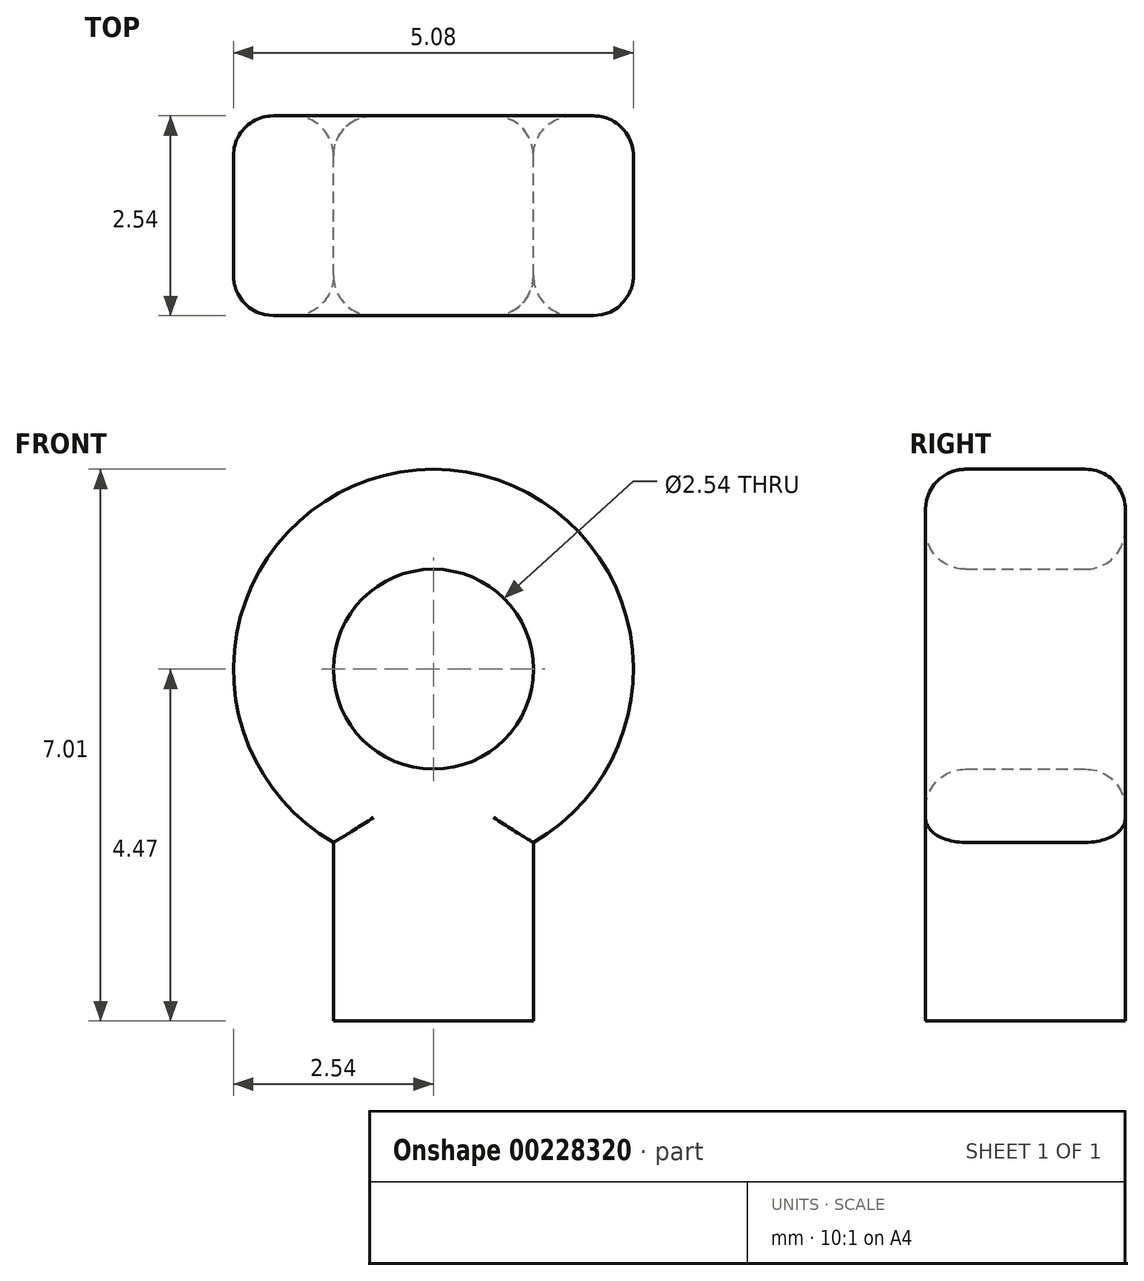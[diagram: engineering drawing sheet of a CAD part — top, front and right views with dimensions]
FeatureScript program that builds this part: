
annotation { "Feature Type Name" : "Feature", "Feature Type Description" : "" }
export const myFeature = defineFeature(function(context is Context, id is Id, definition is map)
    precondition{}
    {
        {
            var Q0;
            Q0=qCreatedBy(makeId("Front.planeOp"),FACE);
            var sketch = newSketch(context, id + "F0", { "sketchPlane" : qUnion([Q0])});
            skArc(sketch, "E0", {"start": v(1.27, -2.2) * mm, "mid": v(0, 2.54) * mm, "end": v(-1.27, -2.2) * mm});
            skCircle(sketch, "E1", {"center": v(0, 0) * mm, "radius": 1.27 * mm});
            skLineSegment(sketch, "E2.0", {"start": v(-1.27, -2.2) * mm, "end": v(-1.27, -4.47) * mm});
            skLineSegment(sketch, "E3.0", {"start": v(1.27, -2.2) * mm, "end": v(1.27, -4.47) * mm});
            skLineSegment(sketch, "E4", {"start": v(-1.27, -4.47) * mm, "end": v(1.27, -4.47) * mm});
            skPoint(sketch, "E5.start.orphan", {"position": v(0, -2.54) * mm});
            skSolve(sketch);
        }
        {
            var Q0;
            Q0=makeQuery(id+"F0.imprint","IMPRINT",FACE,{"disambiguationData":[TD([[makeQuery(id+"F0.imprint","IMPRINT",EDGE,{"derivedFrom":sQuery(id+"F0.wireOp",EDGE,"E0")}),1.0]])]});
            extrude(context, id + "F1", {"entities" : qUnion([Q0]), "depth" : 2.54 * mm});
        }
        {
            var Q0;
            Q0=makeQuery(id+"F1.opExtrude","CAP_EDGE",EDGE,{"disambiguationData":[OSD([sQuery(id+"F0.wireOp",EDGE,"E1")])],"isStart":false});
            var Q1;
            Q1=makeQuery(id+"F1.opExtrude","CAP_EDGE",EDGE,{"disambiguationData":[OSD([sQuery(id+"F0.wireOp",EDGE,"E0")])],"isStart":false});
            var Q2;
            Q2=makeQuery(id+"F1.opExtrude","CAP_EDGE",EDGE,{"disambiguationData":[OSD([sQuery(id+"F0.wireOp",EDGE,"E2.0")])],"isStart":false});
            var Q3;
            Q3=makeQuery(id+"F1.opExtrude","CAP_EDGE",EDGE,{"disambiguationData":[OSD([sQuery(id+"F0.wireOp",EDGE,"E3.0")])],"isStart":false});
            var Q4;
            Q4=makeQuery(id+"F1.opExtrude","CAP_EDGE",EDGE,{"disambiguationData":[OSD([sQuery(id+"F0.wireOp",EDGE,"E1")])],"isStart":true});
            var Q5;
            Q5=makeQuery(id+"F1.opExtrude","CAP_EDGE",EDGE,{"disambiguationData":[OSD([sQuery(id+"F0.wireOp",EDGE,"E0")])],"isStart":true});
            var Q6;
            Q6=makeQuery(id+"F1.opExtrude","CAP_EDGE",EDGE,{"disambiguationData":[OSD([sQuery(id+"F0.wireOp",EDGE,"E2.0")])],"isStart":true});
            var Q7;
            Q7=makeQuery(id+"F1.opExtrude","CAP_EDGE",EDGE,{"disambiguationData":[OSD([sQuery(id+"F0.wireOp",EDGE,"E3.0")])],"isStart":true});
            fillet(context, id + "F2", {"entities" : qUnion([Q0, Q1, Q2, Q3, Q4, Q5, Q6, Q7]), "radius" : 0.5 * mm, "tangentPropagation" : true, "allowEdgeOverflow" : false});
        }
    });
